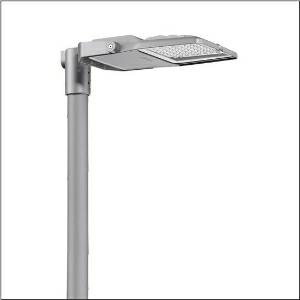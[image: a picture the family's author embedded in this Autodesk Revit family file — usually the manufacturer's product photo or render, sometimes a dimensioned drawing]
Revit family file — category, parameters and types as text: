
# Revit family: floodlight_fl_21_iq_mini___pl61_5xa7772b2c3a_0206
name_source: partatom
category: Lighting Fixtures
units: mm (PartAtom-declared; Revit-internal decimal feet)

## family parameters
Cut with Voids When Loaded = No
Host = Face
Light Source = No
Part Type = Normal
Room Calculation Point = No
Round Connector Dimension = Use Diameter
Shared = No

## types (1)
- --- (1 x LED, 6120 lm, 45.5 W, 3000K)
    Apparent Load = 46 VA
    CIE Flux Codes = 33 65 98 100 100
    Color Rendering = 70
    Color Temperature = 3000K
    Default Elevation = 1800 mm
    Description = Floodlight FL 21 iQ mini, floodlight, primary light control with lens, of PMMA, primary optical cover: protective disc, of toughened safety glass, transparent, light distribution: PL61, light emission: direct distribution, installation type: surface-mounted, LED, High Power LED, rated luminous flux: 6.120lm, luminous efficacy: 135lm/W, light colour: 730, colour temperature: 3000K, control gear: iQ Street-Remote/DALI, control: Auto-Match, Temp-Guard, Night-Set, Smart-Wire, Desk-Remote (wireless, voltage-free reading and setting of iQ features in the workshop via application-optimized NFC function/RFID function), optimised constant luminous flux control (CLO 2.0), Light-Fading, Lumen-Switch, with terminal, 6-pole, mains connection: 220..240V, AC, 50/60Hz, start of lifetime: 46W, end of service life: 48W, reduction: 22W, luminaire housing, of diecast aluminium, powder-coated, Siteco® metallic grey (DB 702S), corrosivity category C5 mid according to DIN EN ISO 12944, suitable for swimming pools, chlorine-resistant, sealing non-destructively replaceable, please order mast flange separately, mast bracket, of steel, galvanised, powder-coated, protection rating (complete): IP66, insulation class (complete): insulation class II (safety insulation), certification: CE, ENEC, VDE, protection symbol: D, impact resistance: IK08, permissible operating ambient temperature: -40..+40°C, permissible operating ambient temperature for outdoor applications: -40..+50°C, standard: DIN EN 12944, LABS conformity tested according to VDMA 24364:2018-05, packaging unit: 1 piece

Light Distribution: PL61
    Height = 70 mm
    Lamp = 1 x LED
    Lamp Light Flux = 6120 lm
    Lamp Power = 45.5 W
    Lamp count = 1
    Length = 485 mm
    Luminous efficacy = 135 lm/W
    Manufacturer = Siteco
    ModVariant = No
    Model = 5XA7772B2C3A
    Number of Poles = 1
    OnlyDefault = Yes
    Power Factor = 1
    Product Name = Floodlight FL 21 iQ mini | PL61
    Product group = floodlight | pylon annexe
    ProductGroupID = 6201
    Protection Class = Protection class II
    Protection Degree = IP 66
    RLX_Detail_Level = 1
    RLX_Emergency_Light_Flux = 0 lm
    RLX_Emergency_Type = 0
    RLX_Emergency_Type_DB = No
    RlxData = <blob elided: 101345 chars, md5=5cef588c>
    Socket = socket
    Standby Power = 0 W
    System Light Flux = 6120 lm
    System Power = 46 W
    Type Comments = factory setting: luminous flux: 100 % | dim-lin: 254 | 463 mA
    Type Image = l_1007125.jpg
    URL = http://relux.com
    VarID = @adj_195057
    Voltage = 0 V
    Weight = 0.00 kg
    Width = 337 mm

## geometry (parser evidence)
native form markers: Blend x4, Sweep x13
no freeform markers — native parametric forms only
